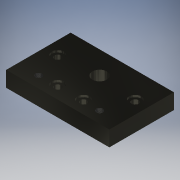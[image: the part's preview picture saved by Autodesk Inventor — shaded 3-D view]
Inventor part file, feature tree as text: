
AUTODESK INVENTOR PART (.ipt)
format: ipt  version: 2019 (Build 230136000, 136)  size: 168,960 bytes
history: native  units: mm
features: sketch x4, extrude x3, thread x2, hole x1
ambient origin geometry x8: Origin, YZ Plane, XZ Plane, XY Plane, X Axis, Y Axis, Z Axis, Center Point
bodies: Solid1 (feature_tree)
feature tree (10):
  extrude  "Extrusion1"  Depth=50.0mm
  extrude  "Extrusion2"  Depth=5.2mm
  thread  "Thread1"  [1 undecoded]
  thread  "Thread2"  [1 undecoded]
  extrude  "Extrusion3"  Depth=10.0mm
  hole  "Hole1"  [1 undecoded]
  sketch  "Sketch1"  dims[d3=80.0mm d4=50.0mm]
  sketch  "Sketch2"  dims[d5=5.2mm d6=5.2mm d7=5.0mm d8=11.18mm]
  sketch  "Sketch3"  dims[d9=10.0mm d10=10.0mm]
  sketch  "Sketch4"  dims[d11=30.0mm d12=30.0mm d13=10.0mm d14=30.0mm d15=30.0mm d16=10.0mm d17=40.0mm d18=32.4mm d19=8.9mm d20=8.9mm d21=16.43mm d23=12.0mm d24=0.0mm d25=9.2mm d26=1.55mm d27=0.0mm d28=10.0mm d29=0.0mm d30=10.0mm d31=0.0mm d32=16.1mm d33=4.5mm d34=0.0mm d35=30.0mm d36=20.0mm d37=4.134mm d38=10.0mm d39=4.0mm d40=2.0mm d41=90.0deg d42=10.0mm d43=0.0mm d44=16.43mm]
note: 3 required parameter values undecoded (feature->parameter linkage not recoverable at this tier; creation-order binding heuristic only, values carry confidence <= 0.55)
